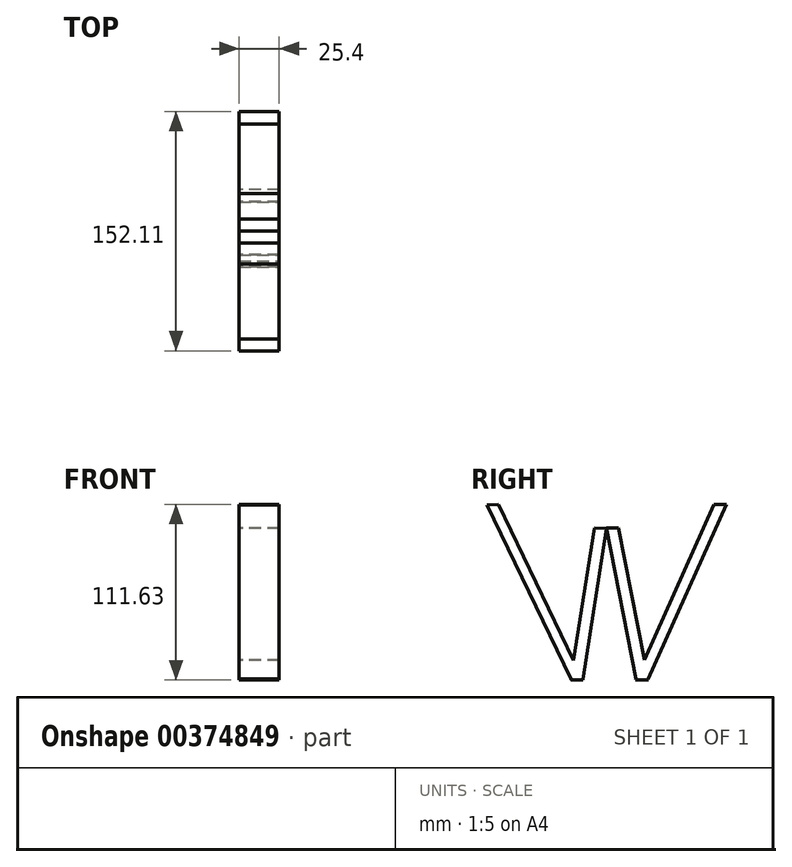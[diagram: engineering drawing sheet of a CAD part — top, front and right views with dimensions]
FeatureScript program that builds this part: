
annotation { "Feature Type Name" : "Feature", "Feature Type Description" : "" }
export const myFeature = defineFeature(function(context is Context, id is Id, definition is map)
    precondition{}
    {
        {
            var Q0;
            Q0=qCreatedBy(makeId("Right.planeOp"),FACE);
            var sketch = newSketch(context, id + "F0", { "sketchPlane" : qUnion([Q0])});
            skLineSegment(sketch, "E0", {"start": v(-76.11, 55.64) * mm, "end": v(-22.6, -55.52) * mm});
            skLineSegment(sketch, "E1", {"start": v(-14.94, -55.52) * mm, "end": v(-68.67, 55.88) * mm});
            skLineSegment(sketch, "E2", {"start": v(-76.11, 55.64) * mm, "end": v(-68.67, 55.88) * mm});
            skLineSegment(sketch, "E3", {"start": v(-22.6, -55.52) * mm, "end": v(-14.94, -55.52) * mm});
            skSolve(sketch);
        }
        {
            var Q0;
            Q0 = qSketchRegion(id + "F0", true);
            extrude(context, id + "F1", {"entities" : qUnion([Q0]), "depth" : 25.4 * mm});
        }
        {
            var Q0;
            Q0=qCreatedBy(makeId("Right.planeOp"),FACE);
            var sketch = newSketch(context, id + "F2", { "sketchPlane" : qUnion([Q0])});
            skLineSegment(sketch, "E4", {"start": v(-15.18, -55.75) * mm, "end": v(0, 40.73) * mm});
            skLineSegment(sketch, "E5", {"start": v(-22.85, -55.28) * mm, "end": v(-7.73, 40.84) * mm});
            skLineSegment(sketch, "E6", {"start": v(0, 40.73) * mm, "end": v(-7.73, 40.84) * mm});
            skLineSegment(sketch, "E7", {"start": v(-15.18, -55.75) * mm, "end": v(-22.85, -55.28) * mm});
            skSolve(sketch);
        }
        {
            var Q0;
            Q0 = qSketchRegion(id + "F2", true);
            extrude(context, id + "F3", {"entities" : qUnion([Q0]), "operationType" : NewBodyOperationType.ADD, "depth" : 25.4 * mm});
        }
        {
            var Q0;
            Q0=qCreatedBy(makeId("Right.planeOp"),FACE);
            var sketch = newSketch(context, id + "F4", { "sketchPlane" : qUnion([Q0])});
            skLineSegment(sketch, "E8", {"start": v(0, 40.84) * mm, "end": v(18.64, -55.75) * mm});
            skLineSegment(sketch, "E9", {"start": v(26.46, -55.75) * mm, "end": v(7.62, 40.84) * mm});
            skLineSegment(sketch, "E10", {"start": v(7.62, 40.84) * mm, "end": v(0, 40.84) * mm});
            skLineSegment(sketch, "E11", {"start": v(26.46, -55.75) * mm, "end": v(18.64, -55.75) * mm});
            skSolve(sketch);
        }
        {
            var Q0;
            Q0 = qSketchRegion(id + "F4", true);
            extrude(context, id + "F5", {"entities" : qUnion([Q0]), "depth" : 25.4 * mm});
        }
        {
            var Q0;
            Q0=qCreatedBy(makeId("Right.planeOp"),FACE);
            var sketch = newSketch(context, id + "F6", { "sketchPlane" : qUnion([Q0])});
            skLineSegment(sketch, "E12", {"start": v(26.23, -55.52) * mm, "end": v(76, 55.88) * mm});
            skLineSegment(sketch, "E13", {"start": v(18.32, -55.52) * mm, "end": v(68.1, 55.88) * mm});
            skLineSegment(sketch, "E14", {"start": v(68.1, 55.88) * mm, "end": v(76, 55.88) * mm});
            skLineSegment(sketch, "E15", {"start": v(26.23, -55.52) * mm, "end": v(18.32, -55.52) * mm});
            skSolve(sketch);
        }
        {
            var Q0;
            Q0 = qSketchRegion(id + "F6", true);
            extrude(context, id + "F7", {"entities" : qUnion([Q0]), "operationType" : NewBodyOperationType.ADD, "depth" : 25.4 * mm});
        }
    });
